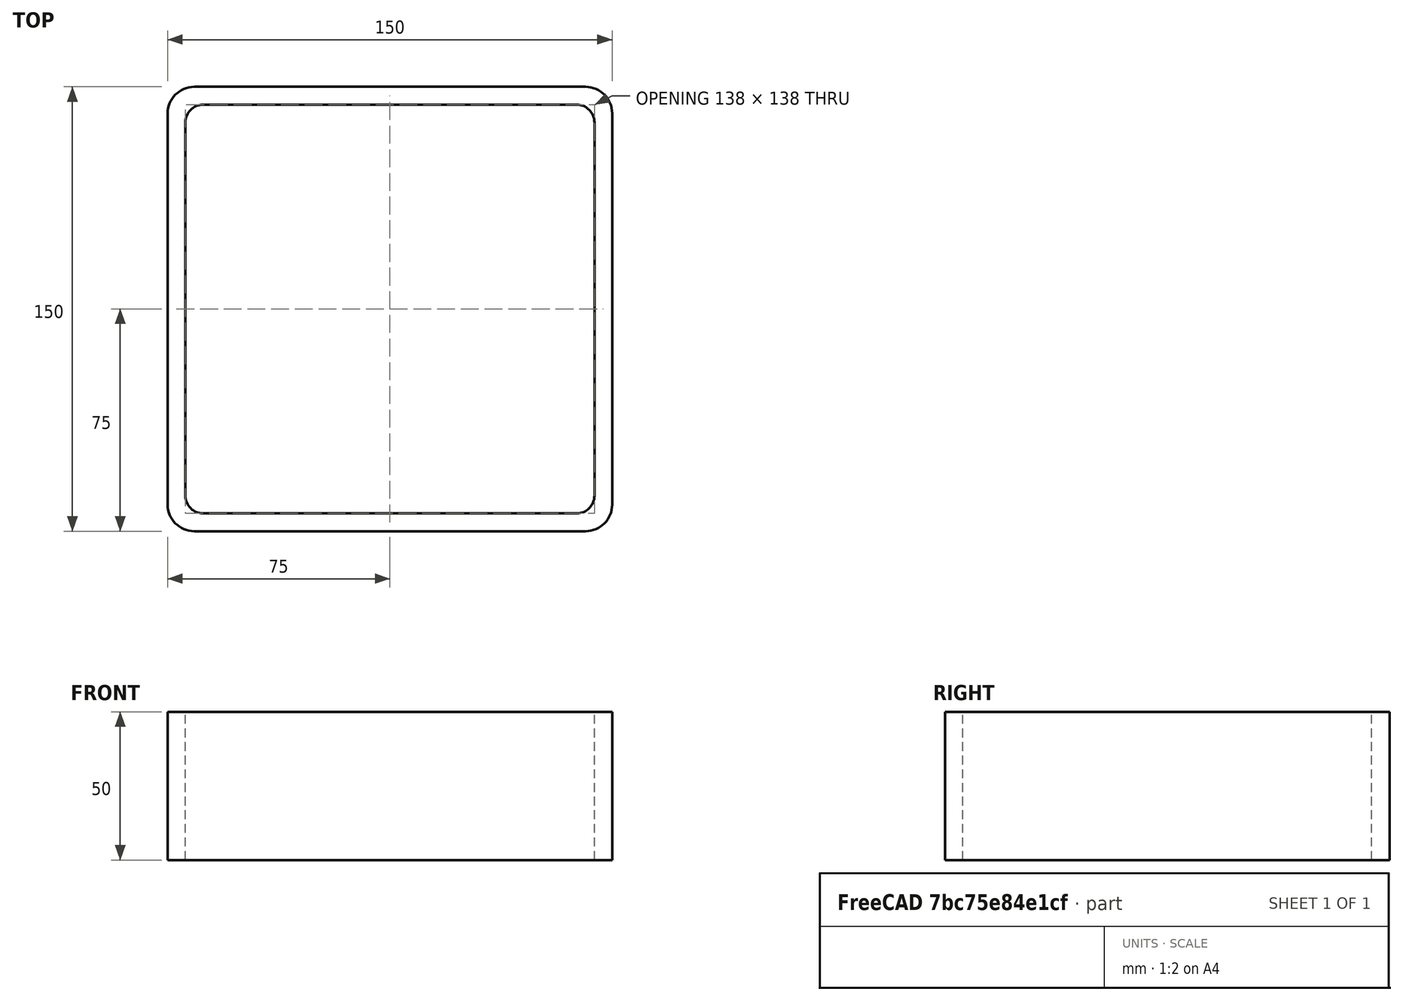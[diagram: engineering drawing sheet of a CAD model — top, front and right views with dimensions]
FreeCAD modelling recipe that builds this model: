
FCSTD DOCUMENT  (FreeCAD 0.15R4671 (Git))
Label: Square hollow section 150x150x6 EN10219 S235JRH
License: All rights reserved
LicenseURL: http://en.wikipedia.org/wiki/All_rights_reserved
objects: Sketcher::SketchObject×1, Part::Extrusion×1
note: 2 computed .brp shape members not serialized (recipe doc carries the construction recipe); baked Part::Feature solids carry a one-line shape summary decoded from their .brp

FEATURE [Sketcher::SketchObject] Sketch
  sketch-geometry (16):
    g0: LineSegment StartX=-63 StartY=69 StartZ=0 EndX=63 EndY=69 EndZ=0
    g1: LineSegment StartX=69 StartY=63 StartZ=0 EndX=69 EndY=-63 EndZ=0
    g2: LineSegment StartX=63 StartY=-69 StartZ=0 EndX=-63 EndY=-69 EndZ=0
    g3: LineSegment StartX=-69 StartY=-63 StartZ=0 EndX=-69 EndY=63 EndZ=0
    g4: LineSegment StartX=-66 StartY=75 StartZ=0 EndX=66 EndY=75 EndZ=0
    g5: LineSegment StartX=75 StartY=66 StartZ=0 EndX=75 EndY=-66 EndZ=0
    g6: LineSegment StartX=66 StartY=-75 StartZ=0 EndX=-66 EndY=-75 EndZ=0
    g7: LineSegment StartX=-75 StartY=-66 StartZ=0 EndX=-75 EndY=66 EndZ=0
    g8: ArcOfCircle CenterX=-63 CenterY=63 CenterZ=0 NormalX=0 NormalY=0 NormalZ=1 Radius=6 StartAngle=1.5708 EndAngle=3.14159
    g9: ArcOfCircle CenterX=63 CenterY=63 CenterZ=0 NormalX=0 NormalY=0 NormalZ=1 Radius=6 StartAngle=0 EndAngle=1.5708
    g10: ArcOfCircle CenterX=63 CenterY=-63 CenterZ=0 NormalX=0 NormalY=0 NormalZ=1 Radius=6 StartAngle=4.71239 EndAngle=6.28319
    g11: ArcOfCircle CenterX=-63 CenterY=-63 CenterZ=0 NormalX=0 NormalY=0 NormalZ=1 Radius=6 StartAngle=3.14159 EndAngle=4.71239
    g12: ArcOfCircle CenterX=66 CenterY=66 CenterZ=0 NormalX=0 NormalY=0 NormalZ=1 Radius=9 StartAngle=0 EndAngle=1.5708
    g13: ArcOfCircle CenterX=66 CenterY=-66 CenterZ=0 NormalX=0 NormalY=0 NormalZ=1 Radius=9 StartAngle=4.71239 EndAngle=6.28319
    g14: ArcOfCircle CenterX=-66 CenterY=-66 CenterZ=0 NormalX=0 NormalY=0 NormalZ=1 Radius=9 StartAngle=3.14159 EndAngle=4.71239
    g15: ArcOfCircle CenterX=-66 CenterY=66 CenterZ=0 NormalX=0 NormalY=0 NormalZ=1 Radius=9 StartAngle=1.5708 EndAngle=3.14159
  constraints (36):
    c: Horizontal(g2)
    c: Vertical(g3)
    c: Horizontal(g6)
    c: Vertical(g7)
    c: Tangent(g3,g8) = 1.5708
    c: Tangent(g0,g8) = 1.5708
    c: Tangent(g0,g9) = 1.5708
    c: Tangent(g1,g9) = 1.5708
    c: Tangent(g1,g10) = 1.5708
    c: Tangent(g2,g10) = 1.5708
    c: Tangent(g2,g11) = 1.5708
    c: Tangent(g3,g11) = 1.5708
    c: Tangent(g4,g12) = 1.5708
    c: Tangent(g5,g12) = 1.5708
    c: Tangent(g5,g13) = 1.5708
    c: Tangent(g6,g13) = 1.5708
    c: Tangent(g6,g14) = 1.5708
    c: Tangent(g7,g14) = 1.5708
    c: Tangent(g7,g15) = 1.5708
    c: Tangent(g4,g15) = 1.5708
    c: Equal(g9,g8)
    c: Equal(g9,g11)
    c: Equal(g9,g10)
    c: Equal(g12,g15)
    c: Equal(g12,g14)
    c: Equal(g12,g13)
    c: Symmetric(g4,g6,g-1)
    c: Symmetric(g7,g5,g-2)
    c: DistanceY(g4,g6) = -150
    c: DistanceX(g7,g5) = 150
    c: Symmetric(g3,g1,g-2)
    c: Symmetric(g0,g2,g-1)
    c: DistanceY(g0,g4) = 6
    c: DistanceX(g5,g1) = -6
    c: Radius(g9) = 6
    c: Radius(g12) = 9
FEATURE [Part::Extrusion] Extrude  label="Square hollow section 150x150x6 EN10219 S235JRH"
  Base = -> Sketch
  Dir = (0,0,50)
  Solid = true
